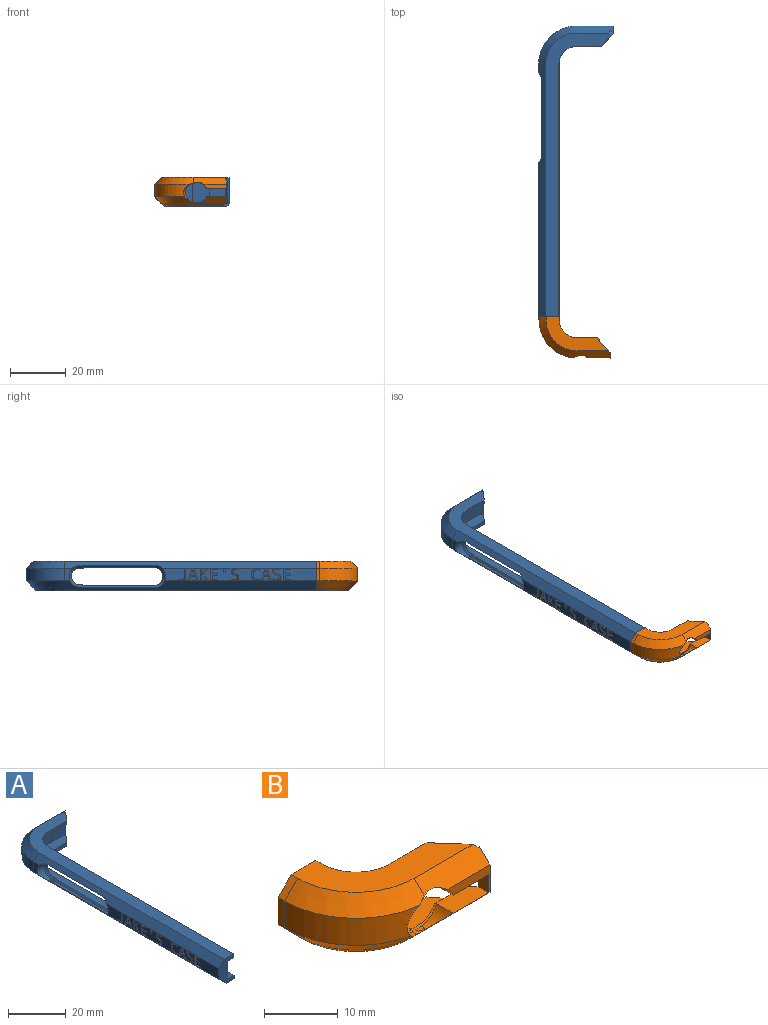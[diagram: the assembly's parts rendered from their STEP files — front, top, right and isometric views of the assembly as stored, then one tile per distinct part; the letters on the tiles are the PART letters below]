
ASSEMBLY  parts=2 mates=1
PART A: 215 faces, bbox 27.9x105.4x11.6 mm
  f0: cone r=2.74mm half-angle=45deg, axis (-1,0,0), area 1.8mm2, adj f2,f3,f25,f29,f204,f213
  f1: cone r=2.74mm half-angle=45deg, axis (-1,0,0), area 15.3mm2, adj f2,f10,f25,f30,f191,f212,f213,f214
  f2: bspline ~24.21x1.5mm, area 25.1mm2, adj f0,f1,f25,f213
  f3: cone r=4.02mm half-angle=45deg, axis (-1,0,0), area 15.3mm2, adj f0,f9,f201,f202,f203,f204,f211,f213
  f4: plane 10.64x7.55mm, normal (0,-1,0), area 44.6mm2, adj f5,f20,f23,f200,f207,f209
  f5: plane 0.96x0.83mm, normal (-0.65,-0.76,0), area 0mm2, adj f4,f6,f23,f209
  f6: plane 9.3x4.81mm, normal (0.76,-0.65,0), area 18.8mm2, adj f5,f20,f22,f23,f28,f35,f43,f187
  f7: plane 0.96x0.83mm, normal (-0.65,-0.76,0), area 0.5mm2, adj f40,f43,f206
  f8: cylinder r=4.24mm len=0.93mm, axis (-1,0,0), area 0.1mm2, adj f9,f31,f38,f190,f191,f201
  f9: cone r=2.74mm half-angle=45deg, axis (-1,0,0), area 1.5mm2, adj f3,f8,f10,f191,f201,f214
  f10: plane 24.21x0.54mm, normal (-0.71,0,0.71), area 18.6mm2, adj f1,f9,f191,f214
  f11: plane 9.26x4.52mm, normal (-1,0,0), area 22.7mm2, adj f18,f19,f44,f45,f46,f47,f48,f49
  f12: plane 26.97x4.53mm, normal (-1,0,0), area 83.9mm2, adj f18,f19,f30,f80,f81,f82,f83,f84
  f13: plane 8.56x4.55mm, normal (-1,0,0), area 26mm2, adj f18,f19,f75,f76,f77,f78,f90,f91
  f14: plane 15.15x4.52mm, normal (-1,0,0), area 56.3mm2, adj f18,f19,f54,f55,f56,f57,f58,f59
  f15: plane 2.38x1.38mm, normal (-1,0,0), area 2.7mm2, adj f19,f175,f181,f182
  f16: plane 2.38x1.38mm, normal (-1,0,0), area 2.7mm2, adj f19,f161,f167,f168
  f17: plane 2.13x1.8mm, normal (-1,0,0), area 2.3mm2, adj f19,f143,f154,f155
  f18: plane 91.1x3.02mm, normal (-0.71,0,0.71), area 281.3mm2, adj f11,f12,f13,f14,f22,f25,f29,f30
  f19: plane 57.25x2.6mm, normal (-0.71,0,-0.71), area 198.6mm2, adj f11,f12,f13,f14,f15,f16,f17,f24
  f20: plane 100.95x21.93mm, normal (0,0,1), area 381.4mm2, adj f4,f6,f35,f36,f37,f196,f199,f200
  f21: plane 100.81x22.43mm, normal (0,0,-1), area 436.2mm2, adj f35,f36,f37,f192,f193,f194,f195,f196
  f22: plane 101.81x23.53mm, normal (0,0,1), area 545.6mm2, adj f6,f18,f26,f27,f28,f41,f42,f196
  f23: plane 100.94x21.93mm, normal (0,0,-1), area 373.5mm2, adj f4,f5,f6,f26,f27,f28,f196,f199
  f24: plane 57.18x0mm, normal (0,0,-1), area 0mm2, adj f19,f30,f190,f196
  f25: plane 27.07x2.41mm, normal (0,0,-1), area 64.9mm2, adj f0,f1,f2,f18,f29,f30
  f26: plane 90.62x1.52mm, normal (1,0,0), area 138.1mm2, adj f22,f23,f27,f196
  f27: cylinder r=6.45mm len=6.46mm, axis (0,0,1), area 15.5mm2, adj f22,f23,f26,f28
  f28: plane 9.01x1.52mm, normal (0,-1,0), area 13.7mm2, adj f6,f22,f23,f27
  f29: cylinder r=4.24mm len=2.17mm, axis (-1,0,0), area 0.1mm2, adj f0,f18,f25,f202
  f30: cylinder r=4.24mm len=8.05mm, axis (-1,0,0), area 26.5mm2, adj f1,f12,f18,f19,f24,f25,f190,f191
  f31: plane 24.24x17.98mm, normal (0,0,-1), area 0.1mm2, adj f8,f38,f39,f40,f188,f189,f190,f197
  f32: plane 13.06x4.49mm, normal (0,1,0), area 58.7mm2, adj f34,f40,f41,f43
  f33: plane 4.49x3mm, normal (-1,0,0), area 9.1mm2, adj f18,f34,f38,f203
  f34: cylinder r=13.72mm len=13.73mm, axis (0,0,-1), area 96.9mm2, adj f32,f33,f39,f42
  f35: plane 8.93x1.5mm, normal (0,-1,0), area 13.4mm2, adj f6,f20,f21,f37,f192
  f36: plane 90.62x1.5mm, normal (1,0,0), area 135.9mm2, adj f20,f21,f37,f196
  f37: cylinder r=6.38mm len=6.38mm, axis (0,0,-1), area 15mm2, adj f20,f21,f35,f36
  f38: plane 7.82x3.57mm, normal (-0.71,0,-0.71), area 12.4mm2, adj f8,f31,f33,f39,f201,f203
  f39: cone r=13.72mm half-angle=45deg, axis (0,0,1), area 70.3mm2, adj f31,f34,f38,f40
  f40: plane 13.06x2.54mm, normal (0,0.71,-0.71), area 46.5mm2, adj f7,f31,f32,f39,f43,f187,f197,f206
  f41: plane 13.06x2.54mm, normal (0,0.71,0.71), area 45.9mm2, adj f22,f32,f42,f43,f198,f205
  f42: cone r=13.72mm half-angle=45deg, axis (0,0,-1), area 70.3mm2, adj f18,f22,f34,f41
  f43: plane 9.57x2.54mm, normal (1,0,0), area 17.9mm2, adj f6,f7,f32,f40,f41,f198
  f44: extruded ~1.07x0.76mm, area 0.9mm2, adj f11,f18,f45,f63,f64
  f45: extruded ~0.83x0.76mm, area 0.7mm2, adj f11,f44,f46,f64
  f46: extruded ~0.8x0.76mm, area 0.7mm2, adj f11,f45,f47,f64
  f47: extruded ~0.91x0.76mm, area 0.8mm2, adj f11,f46,f48,f64
  f48: extruded ~0.87x0.76mm, area 0.7mm2, adj f11,f47,f49,f64
  f49: extruded ~0.76x0.49mm, area 0.4mm2, adj f11,f48,f50,f64
  f50: extruded ~1.07x0.76mm, area 1.1mm2, adj f11,f49,f51,f64
  f51: extruded ~1.26x0.76mm, area 1mm2, adj f11,f50,f52,f64
  f52: plane 0.76x0.54mm, normal (0,-1,0), area 0.4mm2, adj f11,f51,f53,f64
  f53: extruded ~1.26x0.76mm, area 1mm2, adj f11,f19,f52,f54,f64
  f54: extruded ~1.2x0.76mm, area 0.9mm2, adj f14,f19,f53,f55,f64
  f55: extruded ~0.92x0.76mm, area 0.8mm2, adj f14,f54,f56,f64
  f56: extruded ~0.76x0.73mm, area 0.6mm2, adj f14,f55,f57,f64
  f57: extruded ~1x0.76mm, area 0.9mm2, adj f14,f56,f58,f64
  f58: extruded ~0.82x0.76mm, area 0.7mm2, adj f14,f57,f59,f64
  f59: extruded ~0.76x0.5mm, area 0.4mm2, adj f14,f58,f60,f64
  f60: extruded ~0.89x0.76mm, area 1mm2, adj f14,f59,f61,f64
  f61: extruded ~1.1x0.76mm, area 0.9mm2, adj f14,f60,f62,f64
  f62: plane 0.76x0.5mm, normal (0,0.93,0.36), area 0.4mm2, adj f14,f61,f63,f64
  f63: extruded ~1.27x0.76mm, area 1mm2, adj f14,f18,f44,f62,f64
  f64: plane 4.58x2.88mm, normal (-1,0,0), area 5mm2, adj f44,f45,f46,f47,f48,f49,f50,f51
  f65: extruded ~1.09x0.76mm, area 0.8mm2, adj f11,f19,f66,f78,f79
  f66: plane 0.76x0.49mm, normal (0,1,0), area 0.4mm2, adj f11,f65,f67,f79
  f67: extruded ~1x0.76mm, area 0.8mm2, adj f11,f66,f68,f79
  f68: extruded ~1.07x0.76mm, area 0.9mm2, adj f11,f67,f69,f79
  f69: extruded ~1.33x0.76mm, area 1.1mm2, adj f11,f68,f70,f79
  f70: extruded ~1.31x0.76mm, area 1.1mm2, adj f11,f69,f71,f79
  f71: extruded ~1.05x0.76mm, area 0.9mm2, adj f11,f70,f72,f79
  f72: extruded ~0.93x0.76mm, area 0.7mm2, adj f11,f71,f73,f79
  f73: plane 0.76x0.48mm, normal (0,0.89,0.45), area 0.4mm2, adj f11,f72,f74,f79
  f74: extruded ~1.17x0.76mm, area 0.9mm2, adj f11,f18,f73,f75,f79
  f75: extruded ~1.49x0.76mm, area 1.3mm2, adj f13,f18,f74,f76,f79
  f76: extruded ~1.67x0.76mm, area 1.4mm2, adj f13,f75,f77,f79
  f77: extruded ~1.7x0.76mm, area 1.4mm2, adj f13,f76,f78,f79
  f78: extruded ~1.44x0.76mm, area 1.2mm2, adj f13,f19,f65,f77,f79
  f79: plane 4.58x3.2mm, normal (-1,0,0), area 4.5mm2, adj f65,f66,f67,f68,f69,f70,f71,f72
  f80: extruded ~1.07x0.76mm, area 0.9mm2, adj f12,f18,f81,f99,f100
  f81: extruded ~0.83x0.76mm, area 0.7mm2, adj f12,f80,f82,f100
  f82: extruded ~0.8x0.76mm, area 0.7mm2, adj f12,f81,f83,f100
  f83: extruded ~0.91x0.76mm, area 0.8mm2, adj f12,f82,f84,f100
  f84: extruded ~0.87x0.76mm, area 0.7mm2, adj f12,f83,f85,f100
  f85: extruded ~0.76x0.49mm, area 0.4mm2, adj f12,f84,f86,f100
  f86: extruded ~1.07x0.76mm, area 1.1mm2, adj f12,f85,f87,f100
  f87: extruded ~1.26x0.76mm, area 1mm2, adj f12,f86,f88,f100
  f88: plane 0.76x0.54mm, normal (0,-1,0), area 0.4mm2, adj f12,f87,f89,f100
  f89: extruded ~1.26x0.76mm, area 1mm2, adj f12,f19,f88,f90,f100
  f90: extruded ~1.2x0.76mm, area 0.9mm2, adj f13,f19,f89,f91,f100
  f91: extruded ~0.92x0.76mm, area 0.8mm2, adj f13,f90,f92,f100
  f92: extruded ~0.76x0.73mm, area 0.6mm2, adj f13,f91,f93,f100
  f93: extruded ~1x0.76mm, area 0.9mm2, adj f13,f92,f94,f100
  f94: extruded ~0.82x0.76mm, area 0.7mm2, adj f13,f93,f95,f100
  f95: extruded ~0.76x0.5mm, area 0.4mm2, adj f13,f94,f96,f100
  f96: extruded ~0.89x0.76mm, area 1mm2, adj f13,f95,f97,f100
  f97: extruded ~1.1x0.76mm, area 0.9mm2, adj f13,f96,f98,f100
  f98: plane 0.76x0.5mm, normal (0,0.93,0.36), area 0.4mm2, adj f13,f97,f99,f100
  f99: extruded ~1.27x0.76mm, area 1mm2, adj f13,f18,f80,f98,f100
  f100: plane 4.58x2.88mm, normal (-1,0,0), area 5mm2, adj f80,f81,f82,f83,f84,f85,f86,f87
  f101: extruded ~1.15x0.76mm, area 0.9mm2, adj f12,f19,f102,f110,f111
  f102: extruded ~1.05x0.76mm, area 0.9mm2, adj f12,f101,f103,f111
  f103: plane 3.08x0.76mm, normal (0,1,0), area 2.3mm2, adj f12,f102,f104,f111
  f104: plane 0.76x0.57mm, normal (0,0,-1), area 0.4mm2, adj f12,f103,f105,f111
  f105: plane 3.09x0.76mm, normal (0,-1,0), area 2.4mm2, adj f12,f104,f106,f111
  f106: extruded ~0.76x0.69mm, area 0.6mm2, adj f12,f105,f107,f111
  f107: extruded ~0.77x0.76mm, area 0.6mm2, adj f12,f106,f108,f111
  f108: extruded ~0.94x0.76mm, area 0.7mm2, adj f12,f107,f109,f111
  f109: plane 0.76x0.51mm, normal (0,-1,0), area 0.4mm2, adj f12,f108,f110,f111
  f110: extruded ~0.99x0.76mm, area 0.8mm2, adj f12,f19,f101,f109,f111
  f111: plane 4.52x2.57mm, normal (-1,0,0), area 3.3mm2, adj f101,f102,f103,f104,f105,f106,f107,f108
  f112: plane 4.46x0.76mm, normal (0,-1,0), area 3.4mm2, adj f12,f113,f123,f124
  f113: plane 2.57x0.76mm, normal (0,0,1), area 2mm2, adj f19,f112,f114,f124
  f114: plane 0.76x0.5mm, normal (0,1,0), area 0.4mm2, adj f12,f113,f115,f124
  f115: plane 2x0.76mm, normal (0,0,-1), area 1.5mm2, adj f12,f114,f116,f124
  f116: plane 1.58x0.76mm, normal (0,1,0), area 1.2mm2, adj f12,f115,f117,f124
  f117: plane 1.88x0.76mm, normal (0,0,1), area 1.4mm2, adj f12,f116,f118,f124
  f118: plane 0.76x0.49mm, normal (0,1,0), area 0.4mm2, adj f12,f117,f119,f124
  f119: plane 1.88x0.76mm, normal (0,0,-1), area 1.4mm2, adj f12,f118,f120,f124
  f120: plane 1.38x0.76mm, normal (0,1,0), area 1mm2, adj f12,f119,f121,f124
  f121: plane 2x0.76mm, normal (0,0,1), area 1.5mm2, adj f12,f120,f122,f124
  f122: plane 0.76x0.5mm, normal (0,1,0), area 0.4mm2, adj f12,f121,f123,f124
  f123: plane 2.57x0.76mm, normal (0,0,-1), area 2mm2, adj f12,f112,f122,f124
  f124: plane 4.46x2.57mm, normal (-1,0,0), area 5.5mm2, adj f112,f113,f114,f115,f116,f117,f118,f119
  f125: plane 1.61x0.76mm, normal (0,1,0.08), area 1.2mm2, adj f12,f126,f128,f129
  f126: plane 0.76x0.72mm, normal (0,0,-1), area 0.6mm2, adj f12,f125,f127,f129
  f127: plane 1.61x0.76mm, normal (0,-1,0.08), area 1.2mm2, adj f12,f126,f128,f129
  f128: plane 0.76x0.47mm, normal (0,0,1), area 0.4mm2, adj f12,f125,f127,f129
  f129: plane 1.61x0.72mm, normal (-1,0,0), area 1mm2, adj f125,f126,f127,f128
  f130: plane 4.46x0.76mm, normal (0,-1,0), area 3.4mm2, adj f14,f131,f141,f142
  f131: plane 2.57x0.76mm, normal (0,0,1), area 2mm2, adj f19,f130,f132,f142
  f132: plane 0.76x0.5mm, normal (0,1,0), area 0.4mm2, adj f14,f131,f133,f142
  f133: plane 2x0.76mm, normal (0,0,-1), area 1.5mm2, adj f14,f132,f134,f142
  f134: plane 1.58x0.76mm, normal (0,1,0), area 1.2mm2, adj f14,f133,f135,f142
  f135: plane 1.88x0.76mm, normal (0,0,1), area 1.4mm2, adj f14,f134,f136,f142
  f136: plane 0.76x0.49mm, normal (0,1,0), area 0.4mm2, adj f14,f135,f137,f142
  f137: plane 1.88x0.76mm, normal (0,0,-1), area 1.4mm2, adj f14,f136,f138,f142
  f138: plane 1.38x0.76mm, normal (0,1,0), area 1mm2, adj f14,f137,f139,f142
  f139: plane 2x0.76mm, normal (0,0,1), area 1.5mm2, adj f14,f138,f140,f142
  f140: plane 0.76x0.5mm, normal (0,1,0), area 0.4mm2, adj f14,f139,f141,f142
  f141: plane 2.57x0.76mm, normal (0,0,-1), area 2mm2, adj f14,f130,f140,f142
  f142: plane 4.46x2.57mm, normal (-1,0,0), area 5.5mm2, adj f130,f131,f132,f133,f134,f135,f136,f137
  f143: plane 2.13x1.37mm, normal (0,-0.84,0.54), area 1.9mm2, adj f17,f144,f155,f156
  f144: plane 0.76x0.64mm, normal (0,0,1), area 0.5mm2, adj f19,f143,f145,f156
  f145: plane 2.51x1.64mm, normal (0,0.84,-0.55), area 2.3mm2, adj f12,f144,f146,f156
  f146: plane 1.94x1.59mm, normal (0,0.77,0.63), area 1.9mm2, adj f12,f145,f147,f156
  f147: plane 0.76x0.64mm, normal (0,0,-1), area 0.5mm2, adj f12,f146,f148,f156
  f148: plane 1.72x1.38mm, normal (0,-0.78,-0.63), area 1.7mm2, adj f12,f147,f149,f156
  f149: plane 0.76x0.51mm, normal (0,-0.81,-0.58), area 0.5mm2, adj f12,f148,f150,f156
  f150: plane 2.23x0.76mm, normal (0,1,0), area 1.7mm2, adj f12,f149,f151,f156
  f151: plane 0.76x0.57mm, normal (0,0,-1), area 0.4mm2, adj f12,f150,f152,f156
  f152: plane 4.46x0.76mm, normal (0,-1,0), area 3.4mm2, adj f12,f151,f153,f156
  f153: plane 0.76x0.57mm, normal (0,0,1), area 0.4mm2, adj f19,f152,f154,f156
  f154: plane 1.78x0.76mm, normal (0,1,0), area 1.4mm2, adj f17,f153,f155,f156
  f155: plane 0.76x0.43mm, normal (0,0.63,0.78), area 0.4mm2, adj f17,f143,f154,f156
  f156: plane 4.46x3.01mm, normal (-1,0,0), area 5.5mm2, adj f143,f144,f145,f146,f147,f148,f149,f150
  f157: plane 1.29x0.76mm, normal (0,-0.95,0.3), area 1mm2, adj f158,f169,f170,f185
  f158: plane 1.17x0.76mm, normal (0,0,-1), area 0.9mm2, adj f157,f159,f170,f185
  f159: plane 1.42x0.76mm, normal (0,0.96,0.29), area 1.1mm2, adj f158,f160,f170,f185
  f160: extruded ~0.76x0.56mm, area 0.4mm2, adj f159,f169,f170,f185
  f161: plane 1.38x0.76mm, normal (0,-0.95,0.3), area 1.1mm2, adj f16,f162,f168,f170
  f162: plane 0.76x0.59mm, normal (0,0,1), area 0.4mm2, adj f19,f161,f163,f170
  f163: plane 4.47x1.48mm, normal (0,0.95,-0.31), area 3.6mm2, adj f12,f162,f164,f170
  f164: plane 0.76x0.59mm, normal (0,0,-1), area 0.5mm2, adj f12,f163,f165,f170
  f165: plane 4.47x1.47mm, normal (0,-0.95,-0.31), area 3.6mm2, adj f12,f164,f166,f170
  f166: plane 0.76x0.58mm, normal (0,0,1), area 0.4mm2, adj f19,f165,f167,f170
  f167: plane 1.38x0.76mm, normal (0,0.95,0.31), area 1.1mm2, adj f16,f166,f168,f170
  f168: plane 1.5x0.76mm, normal (0,0,1), area 1.1mm2, adj f16,f161,f167,f170
  f169: extruded ~0.76x0.69mm, area 0.5mm2, adj f157,f160,f170,f185
  f170: plane 4.47x3.55mm, normal (-1,0,0), area 5.5mm2, adj f157,f158,f159,f160,f161,f162,f163,f164
  f171: plane 1.29x0.76mm, normal (0,-0.95,0.3), area 1mm2, adj f172,f183,f184,f186
  f172: plane 1.17x0.76mm, normal (0,0,-1), area 0.9mm2, adj f171,f173,f184,f186
  f173: plane 1.42x0.76mm, normal (0,0.96,0.29), area 1.1mm2, adj f172,f174,f184,f186
  f174: extruded ~0.76x0.56mm, area 0.4mm2, adj f173,f183,f184,f186
  f175: plane 1.38x0.76mm, normal (0,-0.95,0.3), area 1.1mm2, adj f15,f176,f182,f184
  f176: plane 0.76x0.59mm, normal (0,0,1), area 0.4mm2, adj f19,f175,f177,f184
  f177: plane 4.47x1.48mm, normal (0,0.95,-0.31), area 3.6mm2, adj f11,f176,f178,f184
  f178: plane 0.76x0.59mm, normal (0,0,-1), area 0.5mm2, adj f11,f177,f179,f184
  f179: plane 4.47x1.47mm, normal (0,-0.95,-0.31), area 3.6mm2, adj f11,f178,f180,f184
  f180: plane 0.76x0.58mm, normal (0,0,1), area 0.4mm2, adj f19,f179,f181,f184
  f181: plane 1.38x0.76mm, normal (0,0.95,0.31), area 1.1mm2, adj f15,f180,f182,f184
  f182: plane 1.5x0.76mm, normal (0,0,1), area 1.1mm2, adj f15,f175,f181,f184
  f183: extruded ~0.76x0.69mm, area 0.5mm2, adj f171,f174,f184,f186
  f184: plane 4.47x3.55mm, normal (-1,0,0), area 5.5mm2, adj f171,f172,f173,f174,f175,f176,f177,f178
  f185: plane 1.98x1.17mm, normal (-1,0,0), area 1.1mm2, adj f157,f158,f159,f160,f169
  f186: plane 1.98x1.17mm, normal (-1,0,0), area 1.1mm2, adj f171,f172,f173,f174,f183
  f187: plane 5.08x4.16mm, normal (0,0,1), area 0.7mm2, adj f6,f40,f188,f192,f197,f206
  f188: plane 13.1x0.28mm, normal (0,1,0), area 0.1mm2, adj f31,f187,f189,f192,f195,f197
  f189: cylinder r=11.18mm len=11.18mm, axis (0,0,-1), area 0.2mm2, adj f31,f188,f190,f194
  f190: plane 90.62x0.28mm, normal (-1,0,0), area 8.2mm2, adj f8,f24,f30,f31,f189,f191,f193,f196
  f191: plane 28.01x1.08mm, normal (0,0,1), area 29.7mm2, adj f1,f8,f9,f10,f30,f190
  f192: plane 4.81x4.16mm, normal (0.76,-0.65,0), area 7.4mm2, adj f21,f35,f187,f188,f195
  f193: plane 90.62x0.99mm, normal (-0.71,0,-0.71), area 127mm2, adj f21,f190,f194,f196
  f194: cone r=10.19mm half-angle=45deg, axis (0,0,1), area 23.5mm2, adj f21,f189,f193,f195
  f195: plane 13.1x0.99mm, normal (0,0.71,-0.71), area 17.7mm2, adj f21,f188,f192,f194
  f196: plane 10.57x7.35mm, normal (0,-1,0), area 44.1mm2, adj f14,f18,f19,f20,f21,f22,f23,f24
  f197: plane 0.32x0.27mm, normal (0.65,0.76,0), area 0.1mm2, adj f31,f40,f187,f188
  f198: plane 0.96x0.83mm, normal (-0.65,-0.76,0), area 0.5mm2, adj f41,f43,f205
  f199: plane 7.55x0.76mm, normal (0,1,0), area 5.7mm2, adj f20,f23,f200,f211,f213,f214
  f200: cylinder r=10.32mm len=10.32mm, axis (0,0,-1), area 122.4mm2, adj f4,f20,f23,f199
  f201: plane 1.15x0.8mm, normal (0,0,1), area 0.6mm2, adj f3,f8,f9,f38,f203
  f202: plane 2.24x0.94mm, normal (0,0,-1), area 2.1mm2, adj f3,f18,f29,f203,f204
  f203: cylinder r=3.87mm len=7.75mm, axis (-1,0,0), area 34mm2, adj f3,f18,f33,f38,f201,f202
  f204: plane 0.22x0.03mm, normal (-1,0,0), area 0mm2, adj f0,f3,f202
  f205: plane 1.67x1.65mm, normal (0.39,0.46,0.8), area 1.7mm2, adj f6,f22,f41,f198
  f206: plane 1.44x1.38mm, normal (0.39,0.46,-0.8), area 1.2mm2, adj f6,f7,f40,f187
  f207: plane 7.53x0.01mm, normal (1,0,0), area 0.1mm2, adj f4,f208,f209
  f208: plane 7.53x6.43mm, normal (0,-1,0), area 48.4mm2, adj f6,f207,f209,f210
  f209: plane 6.43x0.84mm, normal (0,0,-1), area 0.8mm2, adj f4,f5,f6,f207,f208
  f210: plane 6.44x0.85mm, normal (0,0,1), area 0.8mm2, adj f6,f20,f208
  f211: plane 3.14x0.01mm, normal (0,0,1), area 0mm2, adj f3,f199,f213,f214
  f212: plane 55.67x0.01mm, normal (0,0,1), area 0.6mm2, adj f1,f196,f213,f214
  f213: plane 90.62x2.23mm, normal (1,0,0), area 157.4mm2, adj f0,f1,f2,f3,f23,f196,f199,f211
  f214: plane 90.62x5.32mm, normal (1,0,0), area 323.7mm2, adj f1,f3,f9,f10,f20,f196,f199,f211
PART B: 60 faces, bbox 25.9x15.1x10.7 mm
  f0: bspline ~1.15x1.03mm, area 0mm2, adj f11,f45,f57
  f1: plane 22.52x12.42mm, normal (0,0,1), area 114.8mm2, adj f10,f22,f23,f24,f26,f34,f36,f44
  f2: plane 21.62x12.32mm, normal (0,0,-1), area 102.5mm2, adj f10,f24,f26,f34,f40,f44,f45,f46
  f3: plane 7.07x3.41mm, normal (0,0,-1), area 22.4mm2, adj f11,f16,f17,f44,f45,f50
  f4: plane 7.08x3.41mm, normal (0,0,1), area 22.4mm2, adj f6,f15,f19,f38,f39,f50
  f5: plane 11.33x0.99mm, normal (0,-0.71,-0.71), area 15.2mm2, adj f7,f9,f29,f38
  f6: plane 11.79x2.55mm, normal (0,-0.71,-0.71), area 29.3mm2, adj f4,f8,f19,f25,f38,f51
  f7: plane 11.32x0.01mm, normal (0,-1,0), area 0.1mm2, adj f5,f8,f28,f38
  f8: plane 22.52x12.42mm, normal (0,0,-1), area 0mm2, adj f6,f7,f10,f25,f28,f32,f35,f38
  f9: plane 20.62x11.43mm, normal (0,0,-1), area 87.7mm2, adj f5,f10,f21,f27,f29,f30,f31,f38
  f10: plane 10.57x7.35mm, normal (0,1,0), area 38.3mm2, adj f1,f2,f8,f9,f30,f31,f32,f33
  f11: cone r=2.83mm half-angle=45deg, axis (0,-1,0), area 1.9mm2, adj f0,f3,f17,f45
  f12: bspline ~1.15x1.03mm, area 0mm2, adj f15,f43,f58
  f13: plane 1.1x0.04mm, normal (0,-1,0), area 0mm2, adj f14,f19
  f14: plane 1.22x0.79mm, normal (0,0,1), area 0.7mm2, adj f13,f15,f19
  f15: cone r=2.83mm half-angle=45deg, axis (0,-1,0), area 1.9mm2, adj f4,f12,f14,f19,f33,f39,f43
  f16: plane 8.18x4.5mm, normal (0,-1,0), area 11.8mm2, adj f3,f17,f22,f50,f51,f55
  f17: cylinder r=3.83mm len=4.97mm, axis (0,-1,0), area 16.3mm2, adj f3,f11,f16,f18,f22,f57
  f18: bspline ~7.09x3.42mm, area 22.5mm2, adj f17,f19,f20,f23,f25,f59
  f19: cylinder r=3.83mm len=4.97mm, axis (0,-1,0), area 8.2mm2, adj f4,f6,f13,f14,f15,f18,f58
  f20: cylinder r=13.72mm len=13.66mm, axis (0,0,-1), area 83.5mm2, adj f18,f23,f25,f37
  f21: plane 7.13x1.5mm, normal (0,1,0), area 10.7mm2, adj f9,f27,f33,f48
  f22: plane 12.04x2.54mm, normal (0,-0.71,0.71), area 39.4mm2, adj f1,f16,f17,f23,f44,f54,f55
  f23: cone r=13.72mm half-angle=45deg, axis (0,0,-1), area 69.7mm2, adj f1,f18,f20,f22,f36
  f24: plane 7.2x1.52mm, normal (0,1,0), area 11mm2, adj f1,f2,f26,f49
  f25: cone r=13.72mm half-angle=45deg, axis (0,0,1), area 65.2mm2, adj f6,f8,f18,f20,f35
  f26: cylinder r=6.46mm len=6.46mm, axis (0,0,1), area 15.5mm2, adj f1,f2,f24,f34
  f27: cylinder r=6.38mm len=6.38mm, axis (0,0,-1), area 15mm2, adj f9,f21,f30,f33
  f28: cylinder r=11.18mm len=11.19mm, axis (0,0,-1), area 0.2mm2, adj f7,f8,f29,f32
  f29: cone r=10.19mm half-angle=45deg, axis (0,0,1), area 23.5mm2, adj f5,f9,f28,f31
  f30: plane 1.5x1.24mm, normal (1,0,0), area 1.9mm2, adj f9,f10,f27,f33
  f31: plane 1.24x0.99mm, normal (-0.71,0,-0.71), area 1.7mm2, adj f9,f10,f29,f32
  f32: plane 1.24x0.01mm, normal (-1,0,0), area 0mm2, adj f8,f10,f28,f31
  f33: plane 21.73x12.43mm, normal (0,0,1), area 104mm2, adj f10,f15,f21,f27,f30,f38,f39,f42
  f34: plane 1.52x1.24mm, normal (1,0,0), area 1.9mm2, adj f1,f2,f10,f26
  f35: plane 2.54x2.54mm, normal (-0.71,0,-0.71), area 4.5mm2, adj f8,f10,f25,f37
  f36: plane 2.54x2.54mm, normal (-0.71,0,0.71), area 4.5mm2, adj f1,f10,f23,f37
  f37: plane 4.49x1.24mm, normal (-1,0,0), area 5.6mm2, adj f10,f20,f35,f36
  f38: plane 4.45x4.08mm, normal (0.74,0.68,0), area 11.3mm2, adj f4,f5,f6,f7,f8,f9,f33,f39
  f39: plane 8.55x2.04mm, normal (0,1,0), area 13.7mm2, adj f4,f15,f33,f38
  f40: plane 2.23x1.24mm, normal (1,0,0), area 2.8mm2, adj f2,f10,f41,f56
  f41: plane 1.24x0.01mm, normal (0,0,1), area 0mm2, adj f10,f40,f42,f56
  f42: plane 5.32x1.24mm, normal (1,0,0), area 6.6mm2, adj f10,f33,f41,f56
  f43: plane 0.92x0.26mm, normal (0,1,0), area 0.1mm2, adj f12,f15,f33,f58
  f44: plane 4.36x4mm, normal (0.74,0.68,0), area 13.4mm2, adj f1,f2,f3,f22,f45,f46,f54
  f45: plane 10.54x2.48mm, normal (0,1,0), area 18.4mm2, adj f0,f2,f3,f11,f44,f57
  f46: plane 1.52x0.06mm, normal (0.68,-0.74,0), area 0.1mm2, adj f1,f2,f44,f49
  f47: plane 1.5x0.07mm, normal (0.68,-0.74,0), area 0.1mm2, adj f9,f33,f38,f48
  f48: plane 1.5x0.8mm, normal (0.78,0.63,0), area 1.5mm2, adj f9,f21,f33,f47
  f49: plane 1.52x0.8mm, normal (0.78,0.63,0), area 1.6mm2, adj f1,f2,f24,f46
  f50: plane 3.03x2.05mm, normal (-1,0,0), area 6.2mm2, adj f3,f4,f16,f53
  f51: plane 2.05x2.05mm, normal (0,-0.71,-0.71), area 0.7mm2, adj f6,f16,f52,f55
  f52: plane 2.04x0.26mm, normal (0,1,0), area 0.5mm2, adj f38,f51,f53,f55
  f53: plane 3.04x0.25mm, normal (0,1,0), area 0.8mm2, adj f50,f52,f54,f55
  f54: plane 3.51x0.25mm, normal (0,1,0), area 0.9mm2, adj f22,f44,f53,f55
  f55: plane 8.59x2.05mm, normal (1,0,0), area 13.4mm2, adj f16,f22,f51,f52,f53,f54
  f56: plane 7.55x0.76mm, normal (0,-1,0), area 5.7mm2, adj f2,f33,f40,f41,f42,f59
  f57: plane 0.77x0.7mm, normal (-1,0,0), area 0.4mm2, adj f0,f2,f17,f45,f59
  f58: plane 0.77x0.27mm, normal (-1,0,0), area 0mm2, adj f12,f19,f33,f43,f59
  f59: cylinder r=11.08mm len=11.08mm, axis (0,0,-1), area 117.2mm2, adj f2,f18,f33,f56,f57,f58
PLACE A t=(-0.21,-13.97,0.06)mm
PLACE B t=(-0.11,0,0.02)mm
MATE fastened A.f196 <-> B.f10  axis (0,-1,0) through (-43.98,-51.42,6.87)mm
